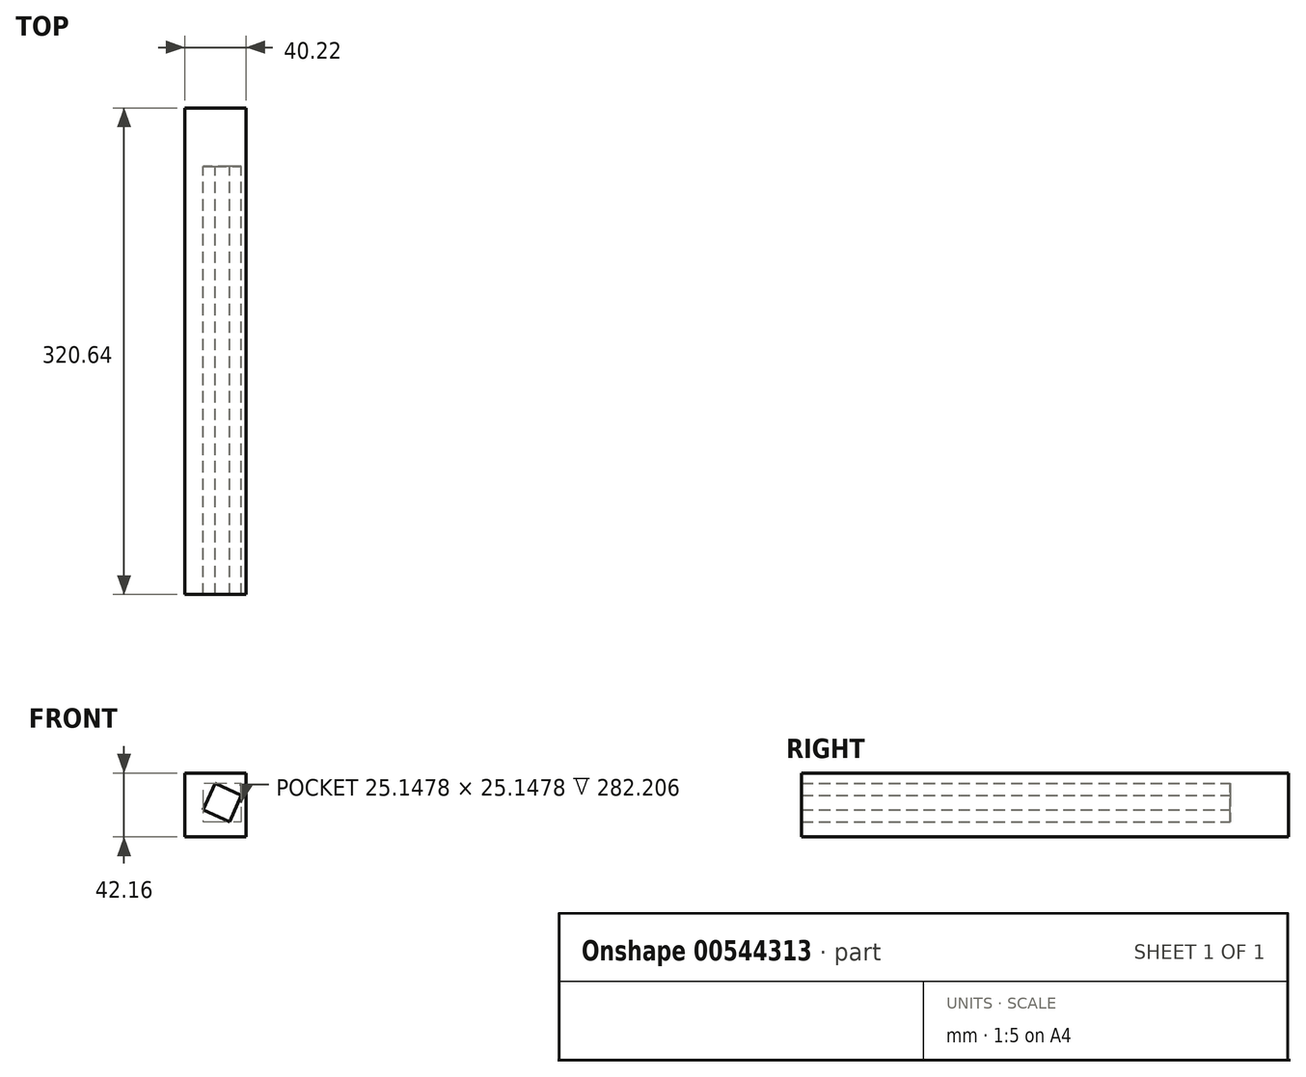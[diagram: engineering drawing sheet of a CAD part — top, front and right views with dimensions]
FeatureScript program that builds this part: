
annotation { "Feature Type Name" : "Feature", "Feature Type Description" : "" }
export const myFeature = defineFeature(function(context is Context, id is Id, definition is map)
    precondition{}
    {
        {
            var Q0;
            Q0=qCreatedBy(makeId("Front.planeOp"),FACE);
            var sketch = newSketch(context, id + "F0", { "sketchPlane" : qUnion([Q0])});
            skLineSegment(sketch, "E0", {"start": v(0, 53) * mm, "end": v(40.22, 53) * mm});
            skLineSegment(sketch, "E1", {"start": v(40.22, 53) * mm, "end": v(40.22, 10.85) * mm});
            skLineSegment(sketch, "E2", {"start": v(40.22, 10.85) * mm, "end": v(0, 10.85) * mm});
            skLineSegment(sketch, "E3", {"start": v(0, 10.85) * mm, "end": v(0, 53) * mm});
            skSolve(sketch);
        }
        {
            var Q0;
            Q0 = qSketchRegion(id + "F0", true);
            extrude(context, id + "F1", {"entities" : qUnion([Q0]), "depth" : 38.43 * mm, "offsetDistance" : 25.4 * mm});
        }
        {
            var Q0;
            Q0=makeQuery(id+"F1.opExtrude","CAP_FACE",FACE,{"disambiguationData":[OSD([sQuery(id+"F0.wireOp",EDGE,"E0"),sQuery(id+"F0.wireOp",EDGE,"E1"),sQuery(id+"F0.wireOp",EDGE,"E2"),sQuery(id+"F0.wireOp",EDGE,"E3")])],"isStart":false});
            var sketch = newSketch(context, id + "F2", { "sketchPlane" : qUnion([Q0])});
            skLineSegment(sketch, "E4.0", {"start": v(0, -6.19) * mm, "end": v(40.22, -6.19) * mm});
            skSolve(sketch);
        }
        {
            var Q0;
            Q0=makeQuery(id+"F2.imprint","IMPRINT",FACE,{"disambiguationData":[TD([[makeQuery(id+"F2.imprint","IMPRINT",EDGE,{"derivedFrom":makeQuery(id+"F1.opExtrude","CAP_EDGE",EDGE,{"disambiguationData":[OSD([sQuery(id+"F0.wireOp",EDGE,"E0")])],"isStart":false})}),-1.0]])]});
            var sketch = newSketch(context, id + "F3", { "sketchPlane" : qUnion([Q0])});
            skCircle(sketch, "E5.cCircle", {"center": v(24.68, 33.49) * mm, "radius": 13.47 * mm, "construction": true});
            skLineSegment(sketch, "E5.0", {"start": v(29.51, 20.91) * mm, "end": v(12.1, 28.66) * mm});
            skLineSegment(sketch, "E5.1", {"start": v(12.1, 28.66) * mm, "end": v(19.85, 46.06) * mm});
            skLineSegment(sketch, "E5.2", {"start": v(19.85, 46.06) * mm, "end": v(37.25, 38.32) * mm});
            skLineSegment(sketch, "E5.3", {"start": v(37.25, 38.32) * mm, "end": v(29.51, 20.91) * mm});
            skSolve(sketch);
        }
        {
            var Q0;
            Q0=makeQuery(id+"F3.imprint","IMPRINT",FACE,{"disambiguationData":[TD([[makeQuery(id+"F3.imprint","IMPRINT",EDGE,{"derivedFrom":sQuery(id+"F3.wireOp",EDGE,"E5.0")}),1.0]])]});
            extrude(context, id + "F4", {"entities" : qUnion([Q0]), "operationType" : NewBodyOperationType.ADD, "depth" : 282.2 * mm, "offsetDistance" : 25.4 * mm});
        }
    });
